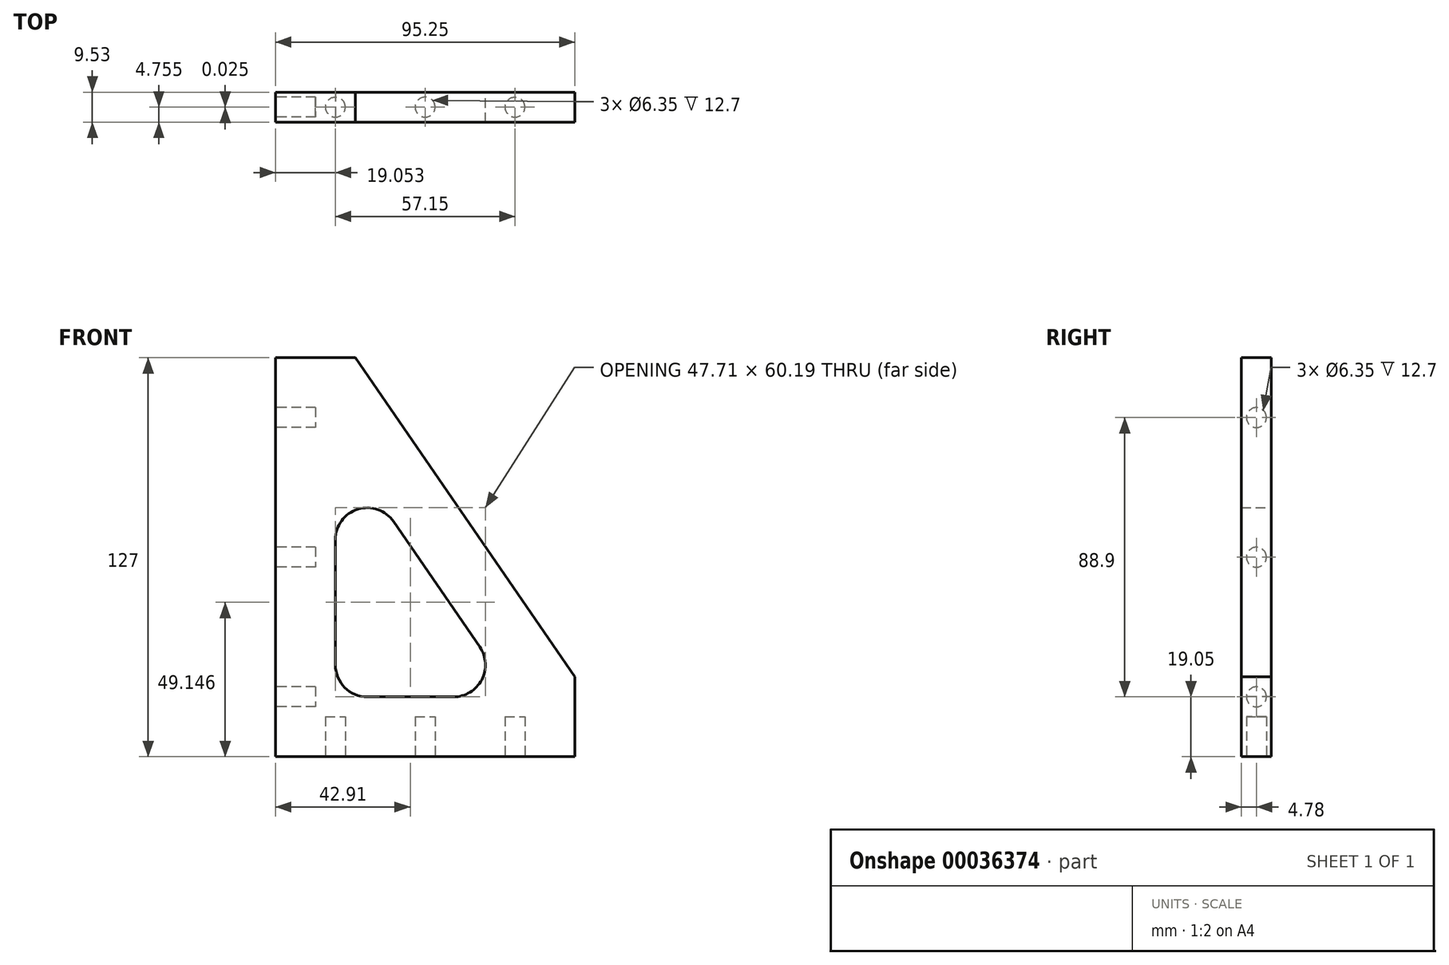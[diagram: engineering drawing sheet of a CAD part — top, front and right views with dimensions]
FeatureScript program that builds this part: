
annotation { "Feature Type Name" : "Feature", "Feature Type Description" : "" }
export const myFeature = defineFeature(function(context is Context, id is Id, definition is map)
    precondition{}
    {
        {
            var Q0;
            Q0=qCreatedBy(makeId("Front.planeOp"),FACE);
            var sketch = newSketch(context, id + "F0", { "sketchPlane" : qUnion([Q0])});
            skLineSegment(sketch, "E0", {"start": v(-75.94, 64.12) * mm, "end": v(-75.94, -62.88) * mm});
            skLineSegment(sketch, "E1", {"start": v(-75.94, -62.88) * mm, "end": v(19.31, -62.88) * mm});
            skLineSegment(sketch, "E2", {"start": v(19.31, -62.88) * mm, "end": v(19.31, -37.48) * mm});
            skLineSegment(sketch, "E3", {"start": v(-75.94, 64.12) * mm, "end": v(-50.54, 64.12) * mm});
            skLineSegment(sketch, "E4", {"start": v(-50.54, 64.12) * mm, "end": v(19.31, -37.48) * mm});
            skSolve(sketch);
        }
        {
            var Q0;
            Q0=makeQuery(id+"F0.imprint","IMPRINT",FACE,{"disambiguationData":[TD([[makeQuery(id+"F0.imprint","IMPRINT",EDGE,{"derivedFrom":sQuery(id+"F0.wireOp",EDGE,"E0")}),1.0]])]});
            extrude(context, id + "F1", {"entities" : qUnion([Q0]), "depth" : 9.52 * mm});
        }
        {
            var Q0;
            Q0=makeQuery(id+"F1.opExtrude","CAP_FACE",FACE,{"disambiguationData":[OSD([sQuery(id+"F0.wireOp",EDGE,"E0"),sQuery(id+"F0.wireOp",EDGE,"E1"),sQuery(id+"F0.wireOp",EDGE,"E2"),sQuery(id+"F0.wireOp",EDGE,"E3"),sQuery(id+"F0.wireOp",EDGE,"E4")])],"isStart":false});
            var sketch = newSketch(context, id + "F2", { "sketchPlane" : qUnion([Q0])});
            skLineSegment(sketch, "E5", {"start": v(-56.89, 38.91) * mm, "end": v(-56.89, -43.83) * mm});
            skLineSegment(sketch, "E6", {"start": v(-56.89, -43.83) * mm, "end": v(0, -43.83) * mm});
            skLineSegment(sketch, "E7", {"start": v(0, -43.83) * mm, "end": v(-56.89, 38.91) * mm});
            skSolve(sketch);
        }
        {
            var Q0;
            Q0 = qSketchRegion(id + "F2", true);
            extrude(context, id + "F3", {"entities" : qUnion([Q0]), "operationType" : NewBodyOperationType.REMOVE, "endBound" : BoundingType.THROUGH_ALL, "oppositeDirection" : true, "depth" : 25.4 * mm});
        }
        {
            var Q0;
            Q0=makeQuery(id+"F3.boolean.opBoolean","COPY",EDGE,{"derivedFrom":makeQuery(id+"F3.opExtrude","SWEPT_EDGE",EDGE,{"disambiguationData":[OSD([sQuery(id+"F2.wireOp",EDGE,"E5"),sQuery(id+"F2.wireOp",EDGE,"E6")])]})});
            var Q1;
            Q1=makeQuery(id+"F3.boolean.opBoolean","COPY",EDGE,{"derivedFrom":makeQuery(id+"F3.opExtrude","SWEPT_EDGE",EDGE,{"disambiguationData":[OSD([sQuery(id+"F2.wireOp",EDGE,"E6"),sQuery(id+"F2.wireOp",EDGE,"E7")])]})});
            var Q2;
            Q2=makeQuery(id+"F3.boolean.opBoolean","COPY",EDGE,{"derivedFrom":makeQuery(id+"F3.opExtrude","SWEPT_EDGE",EDGE,{"disambiguationData":[OSD([sQuery(id+"F2.wireOp",EDGE,"E5"),sQuery(id+"F2.wireOp",EDGE,"E7")])]})});
            fillet(context, id + "F4", {"entities" : qUnion([Q0, Q1, Q2]), "radius" : 10.16 * mm, "tangentPropagation" : true, "allowEdgeOverflow" : false});
        }
        {
            var Q0;
            Q0=makeQuery(id+"F1.opExtrude","SWEPT_FACE",FACE,{"disambiguationData":[OSD([sQuery(id+"F0.wireOp",EDGE,"E1")])]});
            var sketch = newSketch(context, id + "F5", { "sketchPlane" : qUnion([Q0])});
            skCircle(sketch, "E8", {"center": v(-56.89, 4.78) * mm, "radius": 3.18 * mm});
            skCircle(sketch, "E9", {"center": v(-28.31, 4.75) * mm, "radius": 3.18 * mm});
            skCircle(sketch, "E10", {"center": v(0.26, 4.78) * mm, "radius": 3.18 * mm});
            skSolve(sketch);
        }
        {
            var Q0;
            Q0 = qSketchRegion(id + "F5", true);
            extrude(context, id + "F6", {"entities" : qUnion([Q0]), "operationType" : NewBodyOperationType.REMOVE, "oppositeDirection" : true, "depth" : 12.7 * mm});
        }
        {
            var Q0;
            Q0=makeQuery(id+"F1.opExtrude","SWEPT_FACE",FACE,{"disambiguationData":[OSD([sQuery(id+"F0.wireOp",EDGE,"E0")])]});
            var sketch = newSketch(context, id + "F7", { "sketchPlane" : qUnion([Q0])});
            skCircle(sketch, "E11", {"center": v(4.75, 45.07) * mm, "radius": 3.18 * mm});
            skCircle(sketch, "E12", {"center": v(4.75, 0.62) * mm, "radius": 3.18 * mm});
            skCircle(sketch, "E13", {"center": v(4.75, -43.83) * mm, "radius": 3.18 * mm});
            skSolve(sketch);
        }
        {
            var Q0;
            Q0 = qSketchRegion(id + "F7", true);
            extrude(context, id + "F8", {"entities" : qUnion([Q0]), "operationType" : NewBodyOperationType.REMOVE, "oppositeDirection" : true, "depth" : 12.7 * mm});
        }
    });
